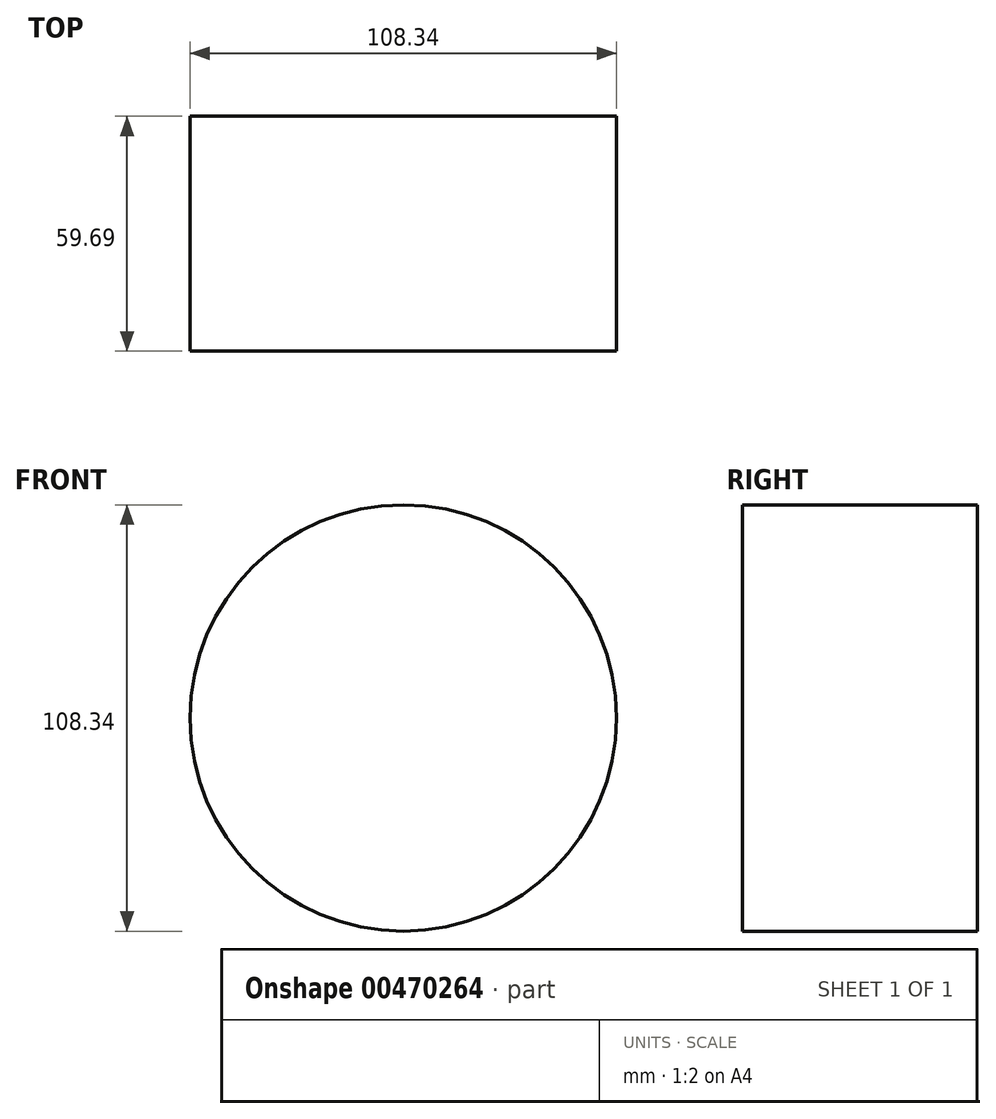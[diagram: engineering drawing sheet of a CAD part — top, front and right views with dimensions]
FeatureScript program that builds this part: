
annotation { "Feature Type Name" : "Feature", "Feature Type Description" : "" }
export const myFeature = defineFeature(function(context is Context, id is Id, definition is map)
    precondition{}
    {
        {
            var Q0;
            Q0=qCreatedBy(makeId("Front.planeOp"),FACE);
            var sketch = newSketch(context, id + "F0", { "sketchPlane" : qUnion([Q0])});
            skCircle(sketch, "E0", {"center": v(-216.82, -56.67) * mm, "radius": 54.17 * mm});
            skSolve(sketch);
        }
        {
            var Q0;
            Q0 = qSketchRegion(id + "F0", true);
            extrude(context, id + "F1", {"entities" : qUnion([Q0]), "depth" : 80 * mm});
        }
        {
            var Q0;
            Q0=makeQuery(id+"F1.opExtrude","CAP_FACE",FACE,{"disambiguationData":[OSD([sQuery(id+"F0.wireOp",EDGE,"E0")])],"isStart":false});
            var sketch = newSketch(context, id + "F2", { "sketchPlane" : qUnion([Q0])});
            skSolve(sketch);
        }
        {
            var Q0;
            Q0=makeQuery(id+"F2.imprint","IMPRINT",FACE,{"disambiguationData":[TD([[makeQuery(id+"F2.imprint","IMPRINT",EDGE,{"derivedFrom":makeQuery(id+"F1.opExtrude","CAP_EDGE",EDGE,{"disambiguationData":[OSD([sQuery(id+"F0.wireOp",EDGE,"E0")])],"isStart":false})}),1.0]])]});
            extrude(context, id + "F3", {"entities" : qUnion([Q0]), "operationType" : NewBodyOperationType.REMOVE, "oppositeDirection" : true, "depth" : 20.32 * mm});
        }
    });
